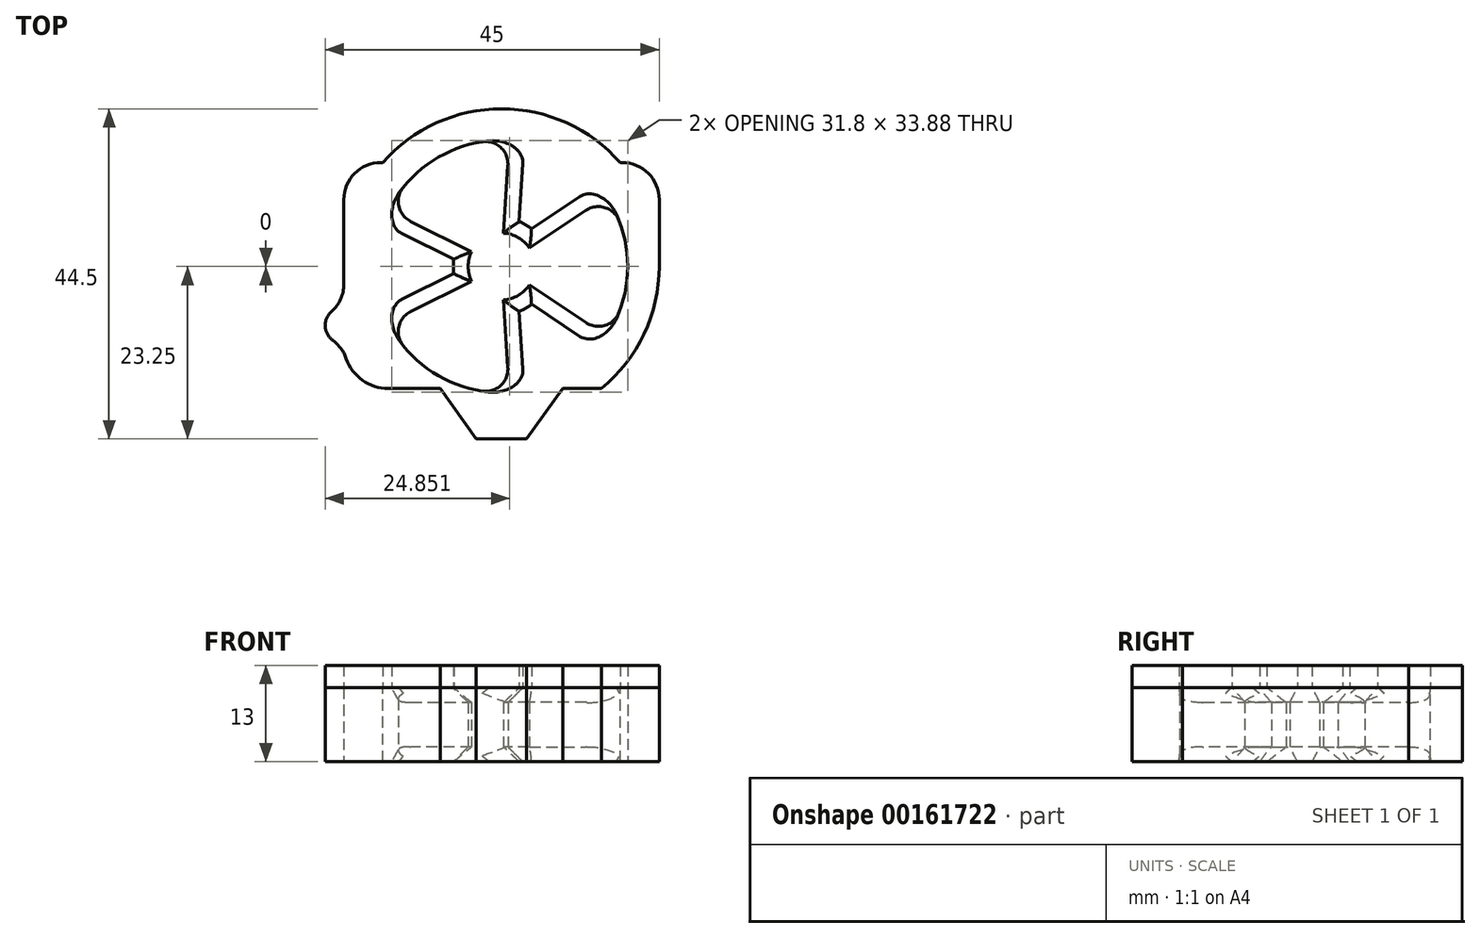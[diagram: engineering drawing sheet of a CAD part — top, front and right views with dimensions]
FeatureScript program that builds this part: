
annotation { "Feature Type Name" : "Feature", "Feature Type Description" : "" }
export const myFeature = defineFeature(function(context is Context, id is Id, definition is map)
    precondition{}
    {
        {
            var Q0;
            Q0=qCreatedBy(makeId("Top.planeOp"),FACE);
            var sketch = newSketch(context, id + "F0", { "sketchPlane" : qUnion([Q0])});
            skCircle(sketch, "E0", {"center": v(0, 0) * mm, "radius": 4.5 * mm});
            skLineSegment(sketch, "E1", {"start": v(0, 0) * mm, "end": v(3.75, -2.5) * mm});
            skLineSegment(sketch, "E2", {"start": v(0, 0) * mm, "end": v(0.28, -4.5) * mm});
            skLineSegment(sketch, "E3", {"start": v(0, 0) * mm, "end": v(2.25, -3.9) * mm, "construction": true});
            skLineSegment(sketch, "E4", {"start": v(2.25, -3.9) * mm, "end": v(3.75, -2.5) * mm, "construction": true});
            skLineSegment(sketch, "E5", {"start": v(2.25, -3.9) * mm, "end": v(0.28, -4.5) * mm, "construction": true});
            skArc(sketch, "E6", {"start": v(14.16, -9.41) * mm, "mid": v(17, 0) * mm, "end": v(14.16, 9.41) * mm});
            skLineSegment(sketch, "E7", {"start": v(0, 0) * mm, "end": v(1.07, -16.97) * mm});
            skLineSegment(sketch, "E8", {"start": v(0, 0) * mm, "end": v(14.16, -9.41) * mm});
            skArc(sketch, "E9", {"start": v(3.4, -20.98) * mm, "mid": v(0, 21.25) * mm, "end": v(-3.4, -20.98) * mm});
            skLineSegment(sketch, "E10.1.0", {"start": v(0, 0) * mm, "end": v(1.07, 16.97) * mm});
            skLineSegment(sketch, "E10.1.1", {"start": v(0, 0) * mm, "end": v(14.16, 9.41) * mm});
            skLineSegment(sketch, "E10.2.0", {"start": v(0, 0) * mm, "end": v(-15.23, -7.56) * mm});
            skLineSegment(sketch, "E10.2.1", {"start": v(0, 0) * mm, "end": v(-15.23, 7.56) * mm});
            skArc(sketch, "E11.trimOffspring", {"start": v(1.07, 16.97) * mm, "mid": v(-8.5, 14.72) * mm, "end": v(-15.23, 7.56) * mm});
            skArc(sketch, "E12.trimOffspring", {"start": v(-15.23, -7.56) * mm, "mid": v(-8.5, -14.72) * mm, "end": v(1.07, -16.97) * mm});
            skPoint(sketch, "E13", {"position": v(-4.03, -2) * mm});
            skLineSegment(sketch, "E14", {"start": v(-3.4, -23.25) * mm, "end": v(3.4, -23.25) * mm});
            skLineSegment(sketch, "E15", {"start": v(-3.4, -23.25) * mm, "end": v(-3.4, -20.98) * mm, "construction": true});
            skLineSegment(sketch, "E16", {"start": v(3.4, -23.25) * mm, "end": v(3.4, -20.98) * mm, "construction": true});
            skLineSegment(sketch, "E17", {"start": v(-8.25, -16.45) * mm, "end": v(8.25, -16.45) * mm, "construction": true});
            skLineSegment(sketch, "E18", {"start": v(-3.4, -23.25) * mm, "end": v(-5.3, -20.58) * mm});
            skLineSegment(sketch, "E19", {"start": v(3.4, -23.25) * mm, "end": v(5.3, -20.58) * mm});
            skLineSegment(sketch, "E20", {"start": v(-3.4, -23.25) * mm, "end": v(-8.25, -16.45) * mm});
            skLineSegment(sketch, "E21", {"start": v(3.4, -23.25) * mm, "end": v(8.25, -16.45) * mm});
            skLineSegment(sketch, "E22", {"start": v(-8.25, -16.45) * mm, "end": v(-13.45, -16.45) * mm});
            skLineSegment(sketch, "E23", {"start": v(8.25, -16.45) * mm, "end": v(13.45, -16.45) * mm});
            skSolve(sketch);
        }
        {
            var Q0;
            {var subQ1=sQuery(id+"F0.wireOp",EDGE,"E6");Q0=makeQuery(id+"F0.imprint","IMPRINT",FACE,{"disambiguationData":[TD([[makeQuery(id+"F0.imprint","IMPRINT",EDGE,{"derivedFrom":subQ1}),-1.0]])]});}
            extrude(context, id + "F1", {"entities" : qUnion([Q0]), "depth" : 10 * mm});
        }
        {
            var Q0;
            {var subQ0=sQuery(id+"F0.wireOp",EDGE,"E0");Q0=makeQuery(id+"F1.opExtrude","CAP_EDGE",EDGE,{"disambiguationData":[OSD([subQ0]),TDD([makeQuery(id+"F0.imprint","IMPRINT",EDGE,{"disambiguationData":[TD([[makeQuery(id+"F0.imprint","INTERSECT",VERTEX,{"derivedFrom":[subQ0,sQuery(id+"F0.wireOp",EDGE,"E10.1.0")]}),1.0]])],"derivedFrom":subQ0})])],"isStart":false});}
            var Q1;
            {var subQ0=sQuery(id+"F0.wireOp",EDGE,"E0");Q1=makeQuery(id+"F1.opExtrude","CAP_EDGE",EDGE,{"disambiguationData":[OSD([subQ0]),TDD([makeQuery(id+"F0.imprint","IMPRINT",EDGE,{"disambiguationData":[TD([[makeQuery(id+"F0.imprint","INTERSECT",VERTEX,{"derivedFrom":[subQ0,sQuery(id+"F0.wireOp",EDGE,"E7")]}),-1.0]])],"derivedFrom":subQ0})])],"isStart":false});}
            var Q2;
            {var subQ0=sQuery(id+"F0.wireOp",EDGE,"E0");Q2=makeQuery(id+"F1.opExtrude","CAP_EDGE",EDGE,{"disambiguationData":[OSD([subQ0]),TDD([makeQuery(id+"F0.imprint","IMPRINT",EDGE,{"disambiguationData":[TD([[makeQuery(id+"F0.imprint","INTERSECT",VERTEX,{"derivedFrom":[subQ0,sQuery(id+"F0.wireOp",EDGE,"E10.2.1")]}),-1.0]])],"derivedFrom":subQ0})])],"isStart":false});}
            var Q3;
            {var subQ0=sQuery(id+"F0.wireOp",EDGE,"E0");Q3=makeQuery(id+"F1.opExtrude","CAP_EDGE",EDGE,{"disambiguationData":[OSD([subQ0]),TDD([makeQuery(id+"F0.imprint","IMPRINT",EDGE,{"disambiguationData":[TD([[makeQuery(id+"F0.imprint","INTERSECT",VERTEX,{"derivedFrom":[subQ0,sQuery(id+"F0.wireOp",EDGE,"E10.1.0")]}),1.0]])],"derivedFrom":subQ0})])],"isStart":true});}
            var Q4;
            {var subQ0=sQuery(id+"F0.wireOp",EDGE,"E0");Q4=makeQuery(id+"F1.opExtrude","CAP_EDGE",EDGE,{"disambiguationData":[OSD([subQ0]),TDD([makeQuery(id+"F0.imprint","IMPRINT",EDGE,{"disambiguationData":[TD([[makeQuery(id+"F0.imprint","INTERSECT",VERTEX,{"derivedFrom":[subQ0,sQuery(id+"F0.wireOp",EDGE,"E10.2.1")]}),-1.0]])],"derivedFrom":subQ0})])],"isStart":true});}
            var Q5;
            {var subQ0=sQuery(id+"F0.wireOp",EDGE,"E0");Q5=makeQuery(id+"F1.opExtrude","CAP_EDGE",EDGE,{"disambiguationData":[OSD([subQ0]),TDD([makeQuery(id+"F0.imprint","IMPRINT",EDGE,{"disambiguationData":[TD([[makeQuery(id+"F0.imprint","INTERSECT",VERTEX,{"derivedFrom":[subQ0,sQuery(id+"F0.wireOp",EDGE,"E7")]}),-1.0]])],"derivedFrom":subQ0})])],"isStart":true});}
            var Q6;
            Q6=makeQuery(id+"F1.opExtrude","CAP_EDGE",EDGE,{"disambiguationData":[OSD([sQuery(id+"F0.wireOp",EDGE,"E8")])],"isStart":false});
            var Q7;
            Q7=makeQuery(id+"F1.opExtrude","CAP_EDGE",EDGE,{"disambiguationData":[OSD([sQuery(id+"F0.wireOp",EDGE,"E7")])],"isStart":false});
            var Q8;
            Q8=makeQuery(id+"F1.opExtrude","CAP_EDGE",EDGE,{"disambiguationData":[OSD([sQuery(id+"F0.wireOp",EDGE,"E10.1.1")])],"isStart":false});
            var Q9;
            Q9=makeQuery(id+"F1.opExtrude","CAP_EDGE",EDGE,{"disambiguationData":[OSD([sQuery(id+"F0.wireOp",EDGE,"E10.1.0")])],"isStart":false});
            var Q10;
            Q10=makeQuery(id+"F1.opExtrude","CAP_EDGE",EDGE,{"disambiguationData":[OSD([sQuery(id+"F0.wireOp",EDGE,"E10.2.0")])],"isStart":false});
            var Q11;
            Q11=makeQuery(id+"F1.opExtrude","CAP_EDGE",EDGE,{"disambiguationData":[OSD([sQuery(id+"F0.wireOp",EDGE,"E10.2.1")])],"isStart":false});
            var Q12;
            Q12=makeQuery(id+"F1.opExtrude","CAP_EDGE",EDGE,{"disambiguationData":[OSD([sQuery(id+"F0.wireOp",EDGE,"E10.1.1")])],"isStart":true});
            var Q13;
            Q13=makeQuery(id+"F1.opExtrude","CAP_EDGE",EDGE,{"disambiguationData":[OSD([sQuery(id+"F0.wireOp",EDGE,"E10.1.0")])],"isStart":true});
            var Q14;
            Q14=makeQuery(id+"F1.opExtrude","CAP_EDGE",EDGE,{"disambiguationData":[OSD([sQuery(id+"F0.wireOp",EDGE,"E10.2.1")])],"isStart":true});
            var Q15;
            Q15=makeQuery(id+"F1.opExtrude","CAP_EDGE",EDGE,{"disambiguationData":[OSD([sQuery(id+"F0.wireOp",EDGE,"E10.2.0")])],"isStart":true});
            var Q16;
            Q16=makeQuery(id+"F1.opExtrude","CAP_EDGE",EDGE,{"disambiguationData":[OSD([sQuery(id+"F0.wireOp",EDGE,"E8")])],"isStart":true});
            var Q17;
            Q17=makeQuery(id+"F1.opExtrude","CAP_EDGE",EDGE,{"disambiguationData":[OSD([sQuery(id+"F0.wireOp",EDGE,"E7")])],"isStart":true});
            chamfer(context, id + "F2", {"entities" : qUnion([Q0, Q1, Q2, Q3, Q4, Q5, Q6, Q7, Q8, Q9, Q10, Q11, Q12, Q13, Q14, Q15, Q16, Q17]), "width" : 2 * mm, "tangentPropagation" : true});
        }
        {
            var Q0;
            Q0=makeQuery(id+"F1.opExtrude","CAP_FACE",FACE,{"disambiguationData":[OSD([sQuery(id+"F0.wireOp",EDGE,"E0"),sQuery(id+"F0.wireOp",EDGE,"E6"),sQuery(id+"F0.wireOp",EDGE,"E7"),sQuery(id+"F0.wireOp",EDGE,"E8"),sQuery(id+"F0.wireOp",EDGE,"E9"),sQuery(id+"F0.wireOp",EDGE,"E10.1.0"),sQuery(id+"F0.wireOp",EDGE,"E10.1.1"),sQuery(id+"F0.wireOp",EDGE,"E10.2.0"),sQuery(id+"F0.wireOp",EDGE,"E10.2.1"),sQuery(id+"F0.wireOp",EDGE,"E11.trimOffspring"),sQuery(id+"F0.wireOp",EDGE,"E12.trimOffspring"),sQuery(id+"F0.wireOp",EDGE,"E14"),sQuery(id+"F0.wireOp",EDGE,"E18"),sQuery(id+"F0.wireOp",EDGE,"E19")])],"isStart":false});
            var sketch = newSketch(context, id + "F3", { "sketchPlane" : qUnion([Q0])});
            skArc(sketch, "E24.0", {"start": v(13.45, -16.45) * mm, "mid": v(0, 21.25) * mm, "end": v(-13.45, -16.45) * mm});
            skLineSegment(sketch, "E25", {"start": v(-15.25, -16.45) * mm, "end": v(-13.45, -16.45) * mm});
            skLineSegment(sketch, "E26", {"start": v(-21.25, 14) * mm, "end": v(-21.25, -5.45) * mm});
            skLineSegment(sketch, "E27", {"start": v(-21.25, 14) * mm, "end": v(-15.99, 14) * mm});
            skPoint(sketch, "E28.visualSharp", {"position": v(-21.25, -16.45) * mm});
            skArc(sketch, "E28.filletArc", {"start": v(-21.25, -10.45) * mm, "mid": v(-19.5, -14.7) * mm, "end": v(-15.25, -16.45) * mm});
            skPoint(sketch, "E29", {"position": v(-21.25, -5.45) * mm});
            skArc(sketch, "E30", {"start": v(-21.25, -5.45) * mm, "mid": v(-23.75, -7.95) * mm, "end": v(-21.25, -10.45) * mm});
            skLineSegment(sketch, "E31.MirrorCS", {"start": v(21.25, 14) * mm, "end": v(15.99, 14) * mm});
            skLineSegment(sketch, "E32.MirrorCS", {"start": v(21.25, 14) * mm, "end": v(21.25, -5.45) * mm});
            skArc(sketch, "E33.MirrorC", {"start": v(21.25, -5.45) * mm, "mid": v(23.75, -7.95) * mm, "end": v(21.25, -10.45) * mm});
            skArc(sketch, "E34.MirrorCS", {"start": v(21.25, -10.45) * mm, "mid": v(19.5, -14.7) * mm, "end": v(15.25, -16.45) * mm});
            skLineSegment(sketch, "E35.MirrorCS", {"start": v(15.25, -16.45) * mm, "end": v(13.45, -16.45) * mm});
            skPoint(sketch, "E36.orphan", {"position": v(21.25, -10.45) * mm});
            skSolve(sketch);
        }
        {
            var Q0;
            {var subQ0=sQuery(id+"F3.wireOp",EDGE,"xTJWEFzh-hfIq-B92l-y43w-CgDuLnQrpT5J");Q0=makeQuery(id+"F3.imprint","IMPRINT",FACE,{"disambiguationData":[TD([[makeQuery(id+"F3.imprint","IMPRINT",EDGE,{"derivedFrom":subQ0}),-1.0]])]});}
            var Q1;
            {var subQ0=sQuery(id+"F3.wireOp",EDGE,"crA4YFTe-ve0g-mP3H-RiMM-CnyTaPhrgKWc");Q1=makeQuery(id+"F3.imprint","IMPRINT",FACE,{"disambiguationData":[TD([[makeQuery(id+"F3.imprint","IMPRINT",EDGE,{"derivedFrom":subQ0}),1.0]])]});}
            var Q2;
            {var subQ0=sQuery(id+"F3.wireOp",EDGE,"efWtnPcA-CMKx-ZpGP-25BT-1YMfhwiBxmS3");Q2=makeQuery(id+"F3.imprint","IMPRINT",FACE,{"disambiguationData":[TD([[makeQuery(id+"F3.imprint","IMPRINT",EDGE,{"derivedFrom":subQ0}),1.0]])]});}
            var Q3;
            {var subQ0=sQuery(id+"F3.wireOp",EDGE,"90cZrt4A-m5NY-ieVN-Iaia-FelK9L81QeNX");Q3=makeQuery(id+"F3.imprint","IMPRINT",FACE,{"disambiguationData":[TD([[makeQuery(id+"F3.imprint","IMPRINT",EDGE,{"derivedFrom":subQ0}),-1.0]])]});}
            var Q4;
            {var subQ0=sQuery(id+"F3.wireOp",EDGE,"E27");Q4=makeQuery(id+"F3.imprint","IMPRINT",FACE,{"disambiguationData":[TD([[makeQuery(id+"F3.imprint","IMPRINT",EDGE,{"derivedFrom":subQ0}),-1.0]])]});}
            var Q5;
            {var subQ0=sQuery(id+"F3.wireOp",EDGE,"E25");Q5=makeQuery(id+"F3.imprint","IMPRINT",FACE,{"disambiguationData":[TD([[makeQuery(id+"F3.imprint","IMPRINT",EDGE,{"derivedFrom":subQ0}),1.0]])]});}
            var Q6;
            {var subQ0=sQuery(id+"F3.wireOp",EDGE,"E33.MirrorC");Q6=makeQuery(id+"F3.imprint","IMPRINT",FACE,{"disambiguationData":[TD([[makeQuery(id+"F3.imprint","IMPRINT",EDGE,{"derivedFrom":subQ0}),-1.0]])]});}
            var Q7;
            {var subQ0=sQuery(id+"F3.wireOp",EDGE,"E31.MirrorCS");Q7=makeQuery(id+"F3.imprint","IMPRINT",FACE,{"disambiguationData":[TD([[makeQuery(id+"F3.imprint","IMPRINT",EDGE,{"derivedFrom":subQ0}),1.0]])]});}
            extrude(context, id + "F4", {"entities" : qUnion([Q0, Q1, Q2, Q3, Q4, Q5, Q6, Q7]), "operationType" : NewBodyOperationType.ADD, "oppositeDirection" : true, "depth" : 10 * mm});
        }
        {
            var Q0;
            Q0=makeQuery(id+"F1.opExtrude","SWEPT_EDGE",EDGE,{"disambiguationData":[OSD([sQuery(id+"F0.wireOp",EDGE,"E10.2.1"),sQuery(id+"F0.wireOp",EDGE,"E11.trimOffspring")])]});
            var Q1;
            Q1=makeQuery(id+"F2.opChamfer","BLEND_EDGE",EDGE,{"blendedFrom":[makeQuery(id+"F1.opExtrude","CAP_EDGE",EDGE,{"disambiguationData":[OSD([sQuery(id+"F0.wireOp",EDGE,"E10.2.1")])],"isStart":false}),makeQuery(id+"F1.opExtrude","SWEPT_FACE",FACE,{"disambiguationData":[OSD([sQuery(id+"F0.wireOp",EDGE,"E11.trimOffspring")])]})],"blendedInto":[makeQuery(id+"F1.opExtrude","SWEPT_FACE",FACE,{"disambiguationData":[OSD([sQuery(id+"F0.wireOp",EDGE,"E11.trimOffspring")])]})]});
            var Q2;
            Q2=makeQuery(id+"F2.opChamfer","BLEND_EDGE",EDGE,{"blendedFrom":[makeQuery(id+"F1.opExtrude","CAP_EDGE",EDGE,{"disambiguationData":[OSD([sQuery(id+"F0.wireOp",EDGE,"E10.2.1")])],"isStart":true}),makeQuery(id+"F1.opExtrude","SWEPT_FACE",FACE,{"disambiguationData":[OSD([sQuery(id+"F0.wireOp",EDGE,"E11.trimOffspring")])]})],"blendedInto":[makeQuery(id+"F1.opExtrude","SWEPT_FACE",FACE,{"disambiguationData":[OSD([sQuery(id+"F0.wireOp",EDGE,"E11.trimOffspring")])]})]});
            var Q3;
            Q3=makeQuery(id+"F2.opChamfer","BLEND_EDGE",EDGE,{"blendedFrom":[makeQuery(id+"F1.opExtrude","CAP_EDGE",EDGE,{"disambiguationData":[OSD([sQuery(id+"F0.wireOp",EDGE,"E10.1.0")])],"isStart":false}),makeQuery(id+"F1.opExtrude","SWEPT_FACE",FACE,{"disambiguationData":[OSD([sQuery(id+"F0.wireOp",EDGE,"E11.trimOffspring")])]})],"blendedInto":[makeQuery(id+"F1.opExtrude","SWEPT_FACE",FACE,{"disambiguationData":[OSD([sQuery(id+"F0.wireOp",EDGE,"E11.trimOffspring")])]})]});
            var Q4;
            Q4=makeQuery(id+"F1.opExtrude","SWEPT_EDGE",EDGE,{"disambiguationData":[OSD([sQuery(id+"F0.wireOp",EDGE,"E10.1.0"),sQuery(id+"F0.wireOp",EDGE,"E11.trimOffspring")])]});
            var Q5;
            Q5=makeQuery(id+"F2.opChamfer","BLEND_EDGE",EDGE,{"blendedFrom":[makeQuery(id+"F1.opExtrude","CAP_EDGE",EDGE,{"disambiguationData":[OSD([sQuery(id+"F0.wireOp",EDGE,"E10.1.0")])],"isStart":true}),makeQuery(id+"F1.opExtrude","SWEPT_FACE",FACE,{"disambiguationData":[OSD([sQuery(id+"F0.wireOp",EDGE,"E11.trimOffspring")])]})],"blendedInto":[makeQuery(id+"F1.opExtrude","SWEPT_FACE",FACE,{"disambiguationData":[OSD([sQuery(id+"F0.wireOp",EDGE,"E11.trimOffspring")])]})]});
            var Q6;
            Q6=makeQuery(id+"F2.opChamfer","BLEND_EDGE",EDGE,{"blendedFrom":[makeQuery(id+"F1.opExtrude","CAP_EDGE",EDGE,{"disambiguationData":[OSD([sQuery(id+"F0.wireOp",EDGE,"E10.1.1")])],"isStart":true}),makeQuery(id+"F1.opExtrude","SWEPT_FACE",FACE,{"disambiguationData":[OSD([sQuery(id+"F0.wireOp",EDGE,"E6")])]})],"blendedInto":[makeQuery(id+"F1.opExtrude","SWEPT_FACE",FACE,{"disambiguationData":[OSD([sQuery(id+"F0.wireOp",EDGE,"E6")])]})]});
            var Q7;
            Q7=makeQuery(id+"F1.opExtrude","SWEPT_EDGE",EDGE,{"disambiguationData":[OSD([sQuery(id+"F0.wireOp",EDGE,"E10.2.0"),sQuery(id+"F0.wireOp",EDGE,"E12.trimOffspring")])]});
            var Q8;
            Q8=makeQuery(id+"F2.opChamfer","BLEND_EDGE",EDGE,{"blendedFrom":[makeQuery(id+"F1.opExtrude","CAP_EDGE",EDGE,{"disambiguationData":[OSD([sQuery(id+"F0.wireOp",EDGE,"E10.2.0")])],"isStart":false}),makeQuery(id+"F1.opExtrude","SWEPT_FACE",FACE,{"disambiguationData":[OSD([sQuery(id+"F0.wireOp",EDGE,"E12.trimOffspring")])]})],"blendedInto":[makeQuery(id+"F1.opExtrude","SWEPT_FACE",FACE,{"disambiguationData":[OSD([sQuery(id+"F0.wireOp",EDGE,"E12.trimOffspring")])]})]});
            var Q9;
            Q9=makeQuery(id+"F1.opExtrude","SWEPT_EDGE",EDGE,{"disambiguationData":[OSD([sQuery(id+"F0.wireOp",EDGE,"E6"),sQuery(id+"F0.wireOp",EDGE,"E10.1.1")])]});
            var Q10;
            Q10=makeQuery(id+"F2.opChamfer","BLEND_EDGE",EDGE,{"blendedFrom":[makeQuery(id+"F1.opExtrude","CAP_EDGE",EDGE,{"disambiguationData":[OSD([sQuery(id+"F0.wireOp",EDGE,"E10.1.1")])],"isStart":false}),makeQuery(id+"F1.opExtrude","SWEPT_FACE",FACE,{"disambiguationData":[OSD([sQuery(id+"F0.wireOp",EDGE,"E6")])]})],"blendedInto":[makeQuery(id+"F1.opExtrude","SWEPT_FACE",FACE,{"disambiguationData":[OSD([sQuery(id+"F0.wireOp",EDGE,"E6")])]})]});
            var Q11;
            Q11=makeQuery(id+"F2.opChamfer","BLEND_EDGE",EDGE,{"blendedFrom":[makeQuery(id+"F1.opExtrude","CAP_EDGE",EDGE,{"disambiguationData":[OSD([sQuery(id+"F0.wireOp",EDGE,"E10.2.0")])],"isStart":true}),makeQuery(id+"F1.opExtrude","SWEPT_FACE",FACE,{"disambiguationData":[OSD([sQuery(id+"F0.wireOp",EDGE,"E12.trimOffspring")])]})],"blendedInto":[makeQuery(id+"F1.opExtrude","SWEPT_FACE",FACE,{"disambiguationData":[OSD([sQuery(id+"F0.wireOp",EDGE,"E12.trimOffspring")])]})]});
            var Q12;
            Q12=makeQuery(id+"F1.opExtrude","SWEPT_EDGE",EDGE,{"disambiguationData":[OSD([sQuery(id+"F0.wireOp",EDGE,"E7"),sQuery(id+"F0.wireOp",EDGE,"E12.trimOffspring")])]});
            var Q13;
            Q13=makeQuery(id+"F2.opChamfer","BLEND_EDGE",EDGE,{"blendedFrom":[makeQuery(id+"F1.opExtrude","CAP_EDGE",EDGE,{"disambiguationData":[OSD([sQuery(id+"F0.wireOp",EDGE,"E7")])],"isStart":false}),makeQuery(id+"F1.opExtrude","SWEPT_FACE",FACE,{"disambiguationData":[OSD([sQuery(id+"F0.wireOp",EDGE,"E12.trimOffspring")])]})],"blendedInto":[makeQuery(id+"F1.opExtrude","SWEPT_FACE",FACE,{"disambiguationData":[OSD([sQuery(id+"F0.wireOp",EDGE,"E12.trimOffspring")])]})]});
            var Q14;
            Q14=makeQuery(id+"F2.opChamfer","BLEND_EDGE",EDGE,{"blendedFrom":[makeQuery(id+"F1.opExtrude","CAP_EDGE",EDGE,{"disambiguationData":[OSD([sQuery(id+"F0.wireOp",EDGE,"E8")])],"isStart":false}),makeQuery(id+"F1.opExtrude","SWEPT_FACE",FACE,{"disambiguationData":[OSD([sQuery(id+"F0.wireOp",EDGE,"E6")])]})],"blendedInto":[makeQuery(id+"F1.opExtrude","SWEPT_FACE",FACE,{"disambiguationData":[OSD([sQuery(id+"F0.wireOp",EDGE,"E6")])]})]});
            var Q15;
            Q15=makeQuery(id+"F1.opExtrude","SWEPT_EDGE",EDGE,{"disambiguationData":[OSD([sQuery(id+"F0.wireOp",EDGE,"E6"),sQuery(id+"F0.wireOp",EDGE,"E8")])]});
            var Q16;
            Q16=makeQuery(id+"F2.opChamfer","BLEND_EDGE",EDGE,{"blendedFrom":[makeQuery(id+"F1.opExtrude","CAP_EDGE",EDGE,{"disambiguationData":[OSD([sQuery(id+"F0.wireOp",EDGE,"E7")])],"isStart":true}),makeQuery(id+"F1.opExtrude","SWEPT_FACE",FACE,{"disambiguationData":[OSD([sQuery(id+"F0.wireOp",EDGE,"E12.trimOffspring")])]})],"blendedInto":[makeQuery(id+"F1.opExtrude","SWEPT_FACE",FACE,{"disambiguationData":[OSD([sQuery(id+"F0.wireOp",EDGE,"E12.trimOffspring")])]})]});
            var Q17;
            Q17=makeQuery(id+"F2.opChamfer","BLEND_EDGE",EDGE,{"blendedFrom":[makeQuery(id+"F1.opExtrude","CAP_EDGE",EDGE,{"disambiguationData":[OSD([sQuery(id+"F0.wireOp",EDGE,"E8")])],"isStart":true}),makeQuery(id+"F1.opExtrude","SWEPT_FACE",FACE,{"disambiguationData":[OSD([sQuery(id+"F0.wireOp",EDGE,"E6")])]})],"blendedInto":[makeQuery(id+"F1.opExtrude","SWEPT_FACE",FACE,{"disambiguationData":[OSD([sQuery(id+"F0.wireOp",EDGE,"E6")])]})]});
            fillet(context, id + "F5", {"entities" : qUnion([Q0, Q1, Q2, Q3, Q4, Q5, Q6, Q7, Q8, Q9, Q10, Q11, Q12, Q13, Q14, Q15, Q16, Q17]), "radius" : 3 * mm, "tangentPropagation" : true, "allowEdgeOverflow" : false});
        }
        {
            var Q0;
            Q0=makeQuery(id+"F4.opExtrude","SWEPT_EDGE",EDGE,{"disambiguationData":[OSD([sQuery(id+"F3.wireOp",EDGE,"E26"),sQuery(id+"F3.wireOp",EDGE,"E27")])]});
            var Q1;
            Q1=makeQuery(id+"F4.opExtrude","SWEPT_EDGE",EDGE,{"disambiguationData":[OSD([sQuery(id+"F3.wireOp",EDGE,"E31.MirrorCS"),sQuery(id+"F3.wireOp",EDGE,"E32.MirrorCS")])]});
            fillet(context, id + "F6", {"entities" : qUnion([Q0, Q1]), "radius" : 5 * mm, "tangentPropagation" : true, "allowEdgeOverflow" : false});
        }
        {
            var Q0;
            Q0=makeQuery(id+"F4.opExtrude","SWEPT_EDGE",EDGE,{"disambiguationData":[OSD([sQuery(id+"F3.wireOp",EDGE,"E28.filletArc"),sQuery(id+"F3.wireOp",EDGE,"E30")])]});
            var Q1;
            Q1=makeQuery(id+"F4.opExtrude","SWEPT_EDGE",EDGE,{"disambiguationData":[OSD([sQuery(id+"F3.wireOp",EDGE,"E26"),sQuery(id+"F3.wireOp",EDGE,"E30")])]});
            var Q2;
            Q2=makeQuery(id+"F4.opExtrude","SWEPT_EDGE",EDGE,{"disambiguationData":[OSD([sQuery(id+"F3.wireOp",EDGE,"E32.MirrorCS"),sQuery(id+"F3.wireOp",EDGE,"E33.MirrorC")])]});
            var Q3;
            Q3=makeQuery(id+"F4.opExtrude","SWEPT_EDGE",EDGE,{"disambiguationData":[OSD([sQuery(id+"F3.wireOp",EDGE,"E33.MirrorC"),sQuery(id+"F3.wireOp",EDGE,"E34.MirrorCS")])]});
            fillet(context, id + "F7", {"entities" : qUnion([Q0, Q1, Q2, Q3]), "radius" : 5 * mm, "tangentPropagation" : true, "allowEdgeOverflow" : false});
        }
        {
            var Q0;
            {var subQ0=sQuery(id+"F3.wireOp",EDGE,"E26");var subQ1=sQuery(id+"F3.wireOp",EDGE,"E24.0");var subQ2=sQuery(id+"F3.wireOp",EDGE,"E32.MirrorCS");Q0=makeQuery(id+"F4.boolean.opBoolean","MERGE",FACE,{"derivedFrom":[makeQuery(id+"F1.opExtrude","CAP_FACE",FACE,{"disambiguationData":[OSD([sQuery(id+"F0.wireOp",EDGE,"E0"),sQuery(id+"F0.wireOp",EDGE,"E6"),sQuery(id+"F0.wireOp",EDGE,"E7"),sQuery(id+"F0.wireOp",EDGE,"E8"),sQuery(id+"F0.wireOp",EDGE,"E9"),sQuery(id+"F0.wireOp",EDGE,"E10.1.0"),sQuery(id+"F0.wireOp",EDGE,"E10.1.1"),sQuery(id+"F0.wireOp",EDGE,"E10.2.0"),sQuery(id+"F0.wireOp",EDGE,"E10.2.1"),sQuery(id+"F0.wireOp",EDGE,"E11.trimOffspring"),sQuery(id+"F0.wireOp",EDGE,"E12.trimOffspring"),sQuery(id+"F0.wireOp",EDGE,"E14"),sQuery(id+"F0.wireOp",EDGE,"E20"),sQuery(id+"F0.wireOp",EDGE,"E21"),sQuery(id+"F0.wireOp",EDGE,"E22"),sQuery(id+"F0.wireOp",EDGE,"E23")])],"isStart":false}),makeQuery(id+"F4.opExtrude","CAP_FACE",FACE,{"disambiguationData":[OSD([subQ1,subQ2,sQuery(id+"F3.wireOp",EDGE,"E33.MirrorC"),sQuery(id+"F3.wireOp",EDGE,"E34.MirrorCS"),sQuery(id+"F3.wireOp",EDGE,"E35.MirrorCS")])],"isStart":true}),makeQuery(id+"F4.opExtrude","CAP_FACE",FACE,{"disambiguationData":[OSD([subQ1,sQuery(id+"F3.wireOp",EDGE,"E31.MirrorCS"),subQ2])],"isStart":true}),makeQuery(id+"F4.opExtrude","CAP_FACE",FACE,{"disambiguationData":[OSD([subQ1,subQ0,sQuery(id+"F3.wireOp",EDGE,"E27")])],"isStart":true}),makeQuery(id+"F4.opExtrude","CAP_FACE",FACE,{"disambiguationData":[OSD([subQ1,sQuery(id+"F3.wireOp",EDGE,"E25"),subQ0,sQuery(id+"F3.wireOp",EDGE,"E28.filletArc"),sQuery(id+"F3.wireOp",EDGE,"E30")])],"isStart":true})]});}
            extrude(context, id + "F8", {"entities" : qUnion([Q0]), "depth" : 3 * mm});
        }
    });
